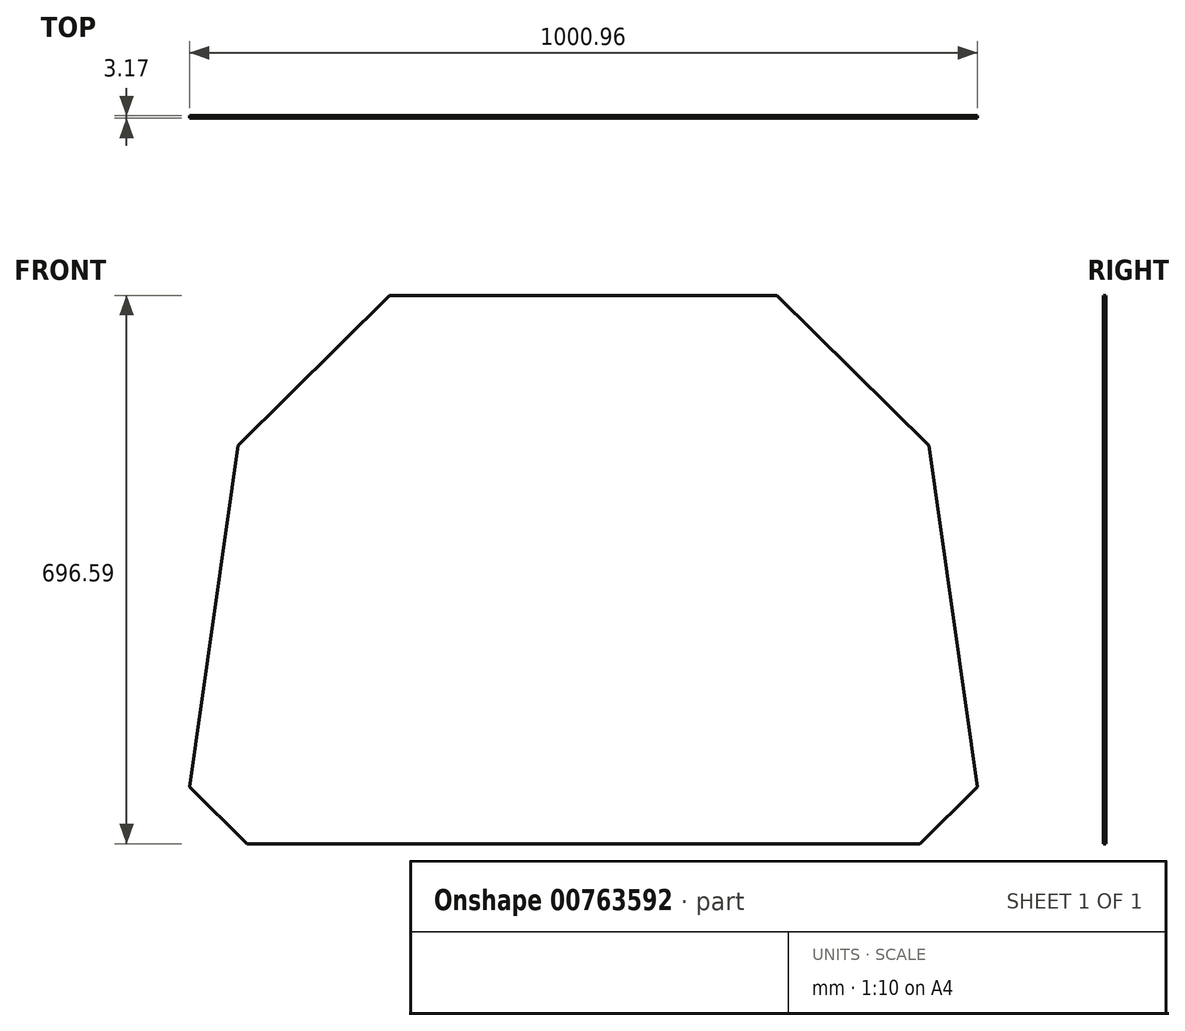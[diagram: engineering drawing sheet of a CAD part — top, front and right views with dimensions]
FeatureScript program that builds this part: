
annotation { "Feature Type Name" : "Feature", "Feature Type Description" : "" }
export const myFeature = defineFeature(function(context is Context, id is Id, definition is map)
    precondition{}
    {
        {
            var Q0;
            Q0=qCreatedBy(makeId("Front.planeOp"),FACE);
            var sketch = newSketch(context, id + "F0", { "sketchPlane" : qUnion([Q0])});
            skLineSegment(sketch, "E0.MirrorCS", {"start": v(-571.59, -206.43) * mm, "end": v(-498.65, -278.59) * mm});
            skLineSegment(sketch, "E1.MirrorCS", {"start": v(356.43, -278.59) * mm, "end": v(-498.65, -278.59) * mm});
            skLineSegment(sketch, "E2.MirrorCS", {"start": v(429.37, -206.43) * mm, "end": v(356.43, -278.59) * mm});
            skLineSegment(sketch, "E3.MirrorCS", {"start": v(367.94, 227.07) * mm, "end": v(429.37, -206.43) * mm});
            skLineSegment(sketch, "E4.MirrorCS", {"start": v(174.94, 418) * mm, "end": v(367.94, 227.07) * mm});
            skLineSegment(sketch, "E5.MirrorCS", {"start": v(174.94, 418) * mm, "end": v(-317.16, 418) * mm});
            skLineSegment(sketch, "E6.MirrorCS", {"start": v(-317.16, 418) * mm, "end": v(-510.16, 227.07) * mm});
            skLineSegment(sketch, "E7.MirrorCS", {"start": v(-510.16, 227.07) * mm, "end": v(-571.59, -206.43) * mm});
            skSolve(sketch);
        }
        {
            var Q0;
            Q0=makeQuery(id+"F0.imprint","IMPRINT",FACE,{"disambiguationData":[TD([[makeQuery(id+"F0.imprint","IMPRINT",EDGE,{"derivedFrom":sQuery(id+"F0.wireOp",EDGE,"E1.MirrorCS")}),-1.0]])]});
            extrude(context, id + "F1", {"entities" : qUnion([Q0]), "depth" : 3.17 * mm, "offsetDistance" : 25.4 * mm});
        }
    });
